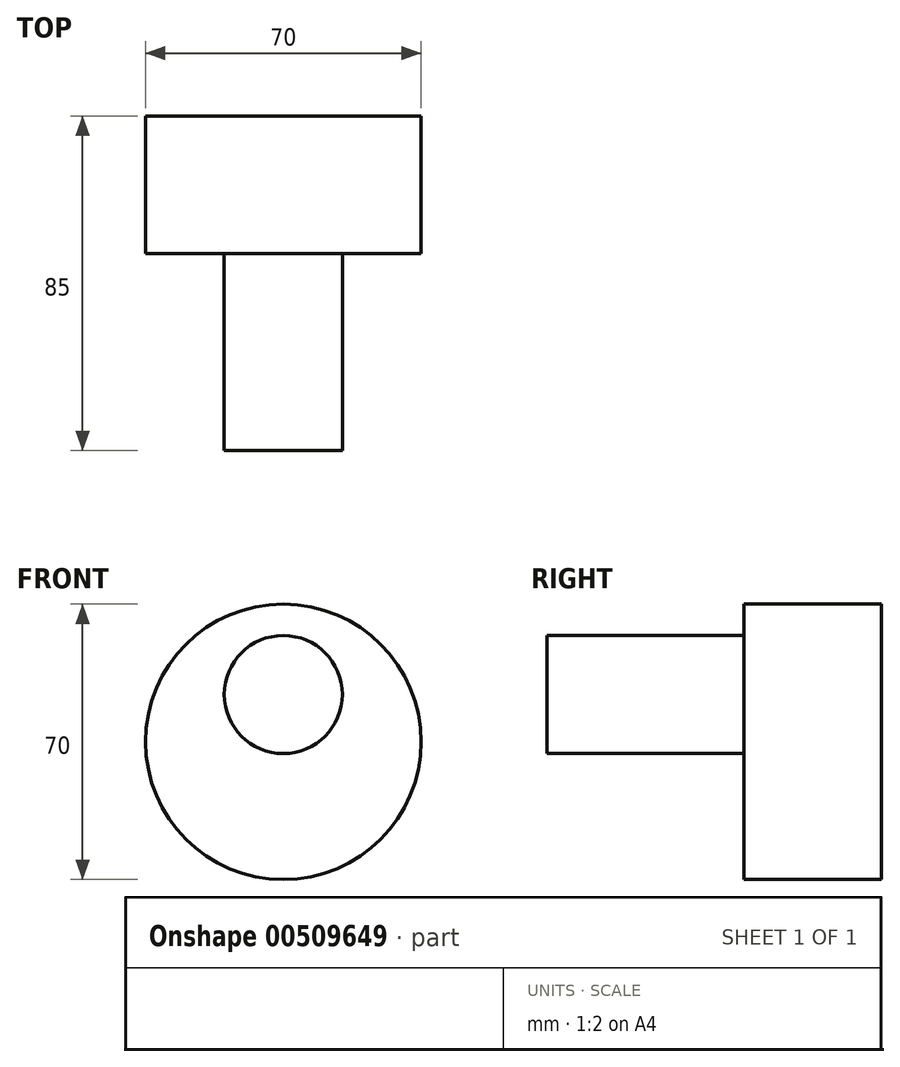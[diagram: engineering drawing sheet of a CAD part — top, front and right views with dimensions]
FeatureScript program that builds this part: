
annotation { "Feature Type Name" : "Feature", "Feature Type Description" : "" }
export const myFeature = defineFeature(function(context is Context, id is Id, definition is map)
    precondition{}
    {
        {
            var Q0;
            Q0=qCreatedBy(makeId("Front.planeOp"),FACE);
            var sketch = newSketch(context, id + "F0", { "sketchPlane" : qUnion([Q0])});
            skCircle(sketch, "E0", {"center": v(0, 0) * mm, "radius": 35 * mm});
            skSolve(sketch);
        }
        {
            var Q0;
            Q0=makeQuery(id+"F0.imprint","IMPRINT",FACE,{"disambiguationData":[TD([[makeQuery(id+"F0.imprint","IMPRINT",EDGE,{"derivedFrom":sQuery(id+"F0.wireOp",EDGE,"E0")}),1.0]])]});
            extrude(context, id + "F1", {"entities" : qUnion([Q0]), "endBound" : BoundingType.SYMMETRIC, "depth" : 35 * mm});
        }
        {
            var Q0;
            Q0=makeQuery(id+"F1.opExtrude","CAP_FACE",FACE,{"disambiguationData":[OSD([sQuery(id+"F0.wireOp",EDGE,"E0")])],"isStart":false});
            var sketch = newSketch(context, id + "F2", { "sketchPlane" : qUnion([Q0])});
            skLineSegment(sketch, "E1", {"start": v(0, 0) * mm, "end": v(0, 35) * mm, "construction": true});
            skCircle(sketch, "E2", {"center": v(0, 12) * mm, "radius": 15 * mm});
            skSolve(sketch);
        }
        {
            var Q0;
            Q0=makeQuery(id+"F2.imprint","IMPRINT",FACE,{"disambiguationData":[TD([[makeQuery(id+"F2.imprint","IMPRINT",EDGE,{"derivedFrom":sQuery(id+"F2.wireOp",EDGE,"E2")}),1.0]])]});
            var Q1;
            Q1=sQuery(id+"F2.wireOp",EDGE,"E2");
            extrude(context, id + "F3", {"entities" : qUnion([Q0]), "operationType" : NewBodyOperationType.ADD, "surfaceEntities" : qUnion([Q1]), "depth" : 50 * mm});
        }
    });
